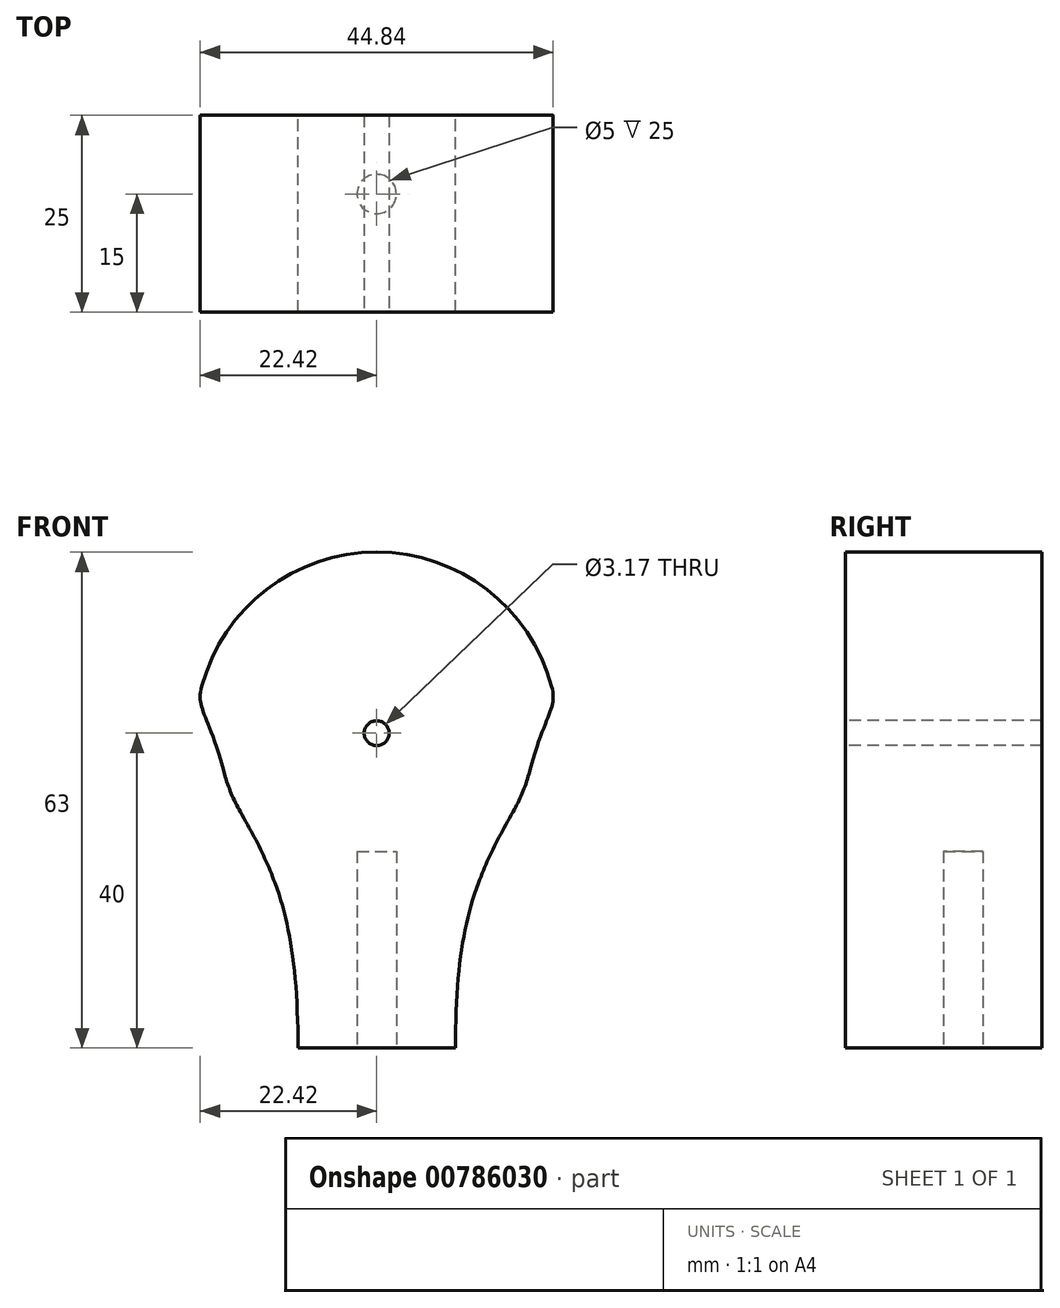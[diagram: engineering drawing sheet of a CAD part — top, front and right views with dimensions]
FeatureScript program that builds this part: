
annotation { "Feature Type Name" : "Feature", "Feature Type Description" : "" }
export const myFeature = defineFeature(function(context is Context, id is Id, definition is map)
    precondition{}
    {
        {
            var Q0;
            Q0=qCreatedBy(makeId("Front.planeOp"),FACE);
            var sketch = newSketch(context, id + "F0", { "sketchPlane" : qUnion([Q0])});
            skLineSegment(sketch, "E0.bottom", {"start": v(10, 0) * mm, "end": v(-10, 0) * mm, "construction": true});
            skLineSegment(sketch, "E0.top", {"start": v(10, -40) * mm, "end": v(-10, -40) * mm});
            skLineSegment(sketch, "E0.left", {"start": v(10, 0) * mm, "end": v(10, -40) * mm, "construction": true});
            skLineSegment(sketch, "E0.right", {"start": v(-10, 0) * mm, "end": v(-10, -40) * mm, "construction": true});
            skPoint(sketch, "E0.middle", {"position": v(0, -20) * mm});
            skCircle(sketch, "E1", {"center": v(0, 0) * mm, "radius": 20 * mm});
            skCircle(sketch, "E2", {"center": v(0, 0) * mm, "radius": 23 * mm});
            skLineSegment(sketch, "E3", {"start": v(0, 0) * mm, "end": v(22.22, 5.95) * mm});
            skLineSegment(sketch, "E4", {"start": v(0, 0) * mm, "end": v(19.32, -5.18) * mm});
            skLineSegment(sketch, "E5", {"start": v(0, 0) * mm, "end": v(17.32, -10) * mm});
            skLineSegment(sketch, "E6", {"start": v(0, 0) * mm, "end": v(19.92, 11.5) * mm});
            skFitSpline(sketch, "E7", {"points": [v(19.32, -5.18) * mm, v(22.22, 5.95) * mm], "startDerivative": vector(6.21, 23.18) * mm, "endDerivative": vector(-2.33, 8.7) * mm});
            skLineSegment(sketch, "E8", {"start": v(22.22, 5.95) * mm, "end": v(23, 3.06) * mm});
            skLineSegment(sketch, "E9", {"start": v(19.32, -5.18) * mm, "end": v(21.39, 2.55) * mm});
            skFitSpline(sketch, "E10", {"points": [v(17.32, -10) * mm, v(10, -40) * mm], "startDerivative": vector(-15, -25.98) * mm, "endDerivative": vector(0, -45) * mm});
            skLineSegment(sketch, "E11", {"start": v(17.32, -10) * mm, "end": v(12.32, -18.66) * mm});
            skLineSegment(sketch, "E12", {"start": v(0, -40) * mm, "end": v(0, 23) * mm, "construction": true});
            skFitSpline(sketch, "E13.MirrorCS", {"points": [v(-19.32, -5.18) * mm, v(-22.22, 5.95) * mm], "startDerivative": vector(-6.21, 23.18) * mm, "endDerivative": vector(2.33, 8.7) * mm});
            skFitSpline(sketch, "E14.MirrorCS", {"points": [v(-17.32, -10) * mm, v(-10, -40) * mm], "startDerivative": vector(15, -25.98) * mm, "endDerivative": vector(0, -45) * mm});
            skLineSegment(sketch, "E15.MirrorCS", {"start": v(0, 0) * mm, "end": v(-19.92, 11.5) * mm});
            skSolve(sketch);
        }
        {
            var Q0;
            {var subQ0=sQuery(id+"F0.wireOp",EDGE,"E6");var subQ1=sQuery(id+"F0.wireOp",EDGE,"E1");var subQ2=makeQuery(id+"F0.imprint","INTERSECT",VERTEX,{"derivedFrom":[subQ1,subQ0]});Q0=makeQuery(id+"F0.imprint","IMPRINT",FACE,{"disambiguationData":[TD([[makeQuery(id+"F0.imprint","IMPRINT",EDGE,{"disambiguationData":[TD([[subQ2,-1.0]])],"derivedFrom":subQ1}),1.0]])]});}
            var Q1;
            {var subQ0=sQuery(id+"F0.wireOp",EDGE,"E6");var subQ1=sQuery(id+"F0.wireOp",EDGE,"E1");var subQ2=makeQuery(id+"F0.imprint","INTERSECT",VERTEX,{"derivedFrom":[subQ1,subQ0]});Q1=makeQuery(id+"F0.imprint","IMPRINT",FACE,{"disambiguationData":[TD([[makeQuery(id+"F0.imprint","IMPRINT",EDGE,{"disambiguationData":[TD([[subQ2,-1.0]])],"derivedFrom":subQ1}),-1.0]])]});}
            var Q2;
            {var subQ0=sQuery(id+"F0.wireOp",EDGE,"E6");var subQ1=sQuery(id+"F0.wireOp",EDGE,"E1");var subQ2=makeQuery(id+"F0.imprint","INTERSECT",VERTEX,{"derivedFrom":[subQ1,subQ0]});Q2=makeQuery(id+"F0.imprint","IMPRINT",FACE,{"disambiguationData":[TD([[makeQuery(id+"F0.imprint","IMPRINT",EDGE,{"disambiguationData":[TD([[subQ2,1.0]])],"derivedFrom":subQ1}),-1.0]])]});}
            var Q3;
            {var subQ0=sQuery(id+"F0.wireOp",EDGE,"E6");var subQ1=sQuery(id+"F0.wireOp",EDGE,"E1");var subQ2=makeQuery(id+"F0.imprint","INTERSECT",VERTEX,{"derivedFrom":[subQ1,subQ0]});Q3=makeQuery(id+"F0.imprint","IMPRINT",FACE,{"disambiguationData":[TD([[makeQuery(id+"F0.imprint","IMPRINT",EDGE,{"disambiguationData":[TD([[subQ2,1.0]])],"derivedFrom":subQ1}),1.0]])]});}
            var Q4;
            {var subQ0=sQuery(id+"F0.wireOp",EDGE,"E4");Q4=makeQuery(id+"F0.imprint","IMPRINT",FACE,{"disambiguationData":[TD([[makeQuery(id+"F0.imprint","IMPRINT",EDGE,{"derivedFrom":subQ0}),1.0]])]});}
            var Q5;
            {var subQ0=sQuery(id+"F0.wireOp",EDGE,"E7");Q5=makeQuery(id+"F0.imprint","IMPRINT",FACE,{"disambiguationData":[TD([[makeQuery(id+"F0.imprint","IMPRINT",EDGE,{"derivedFrom":subQ0}),1.0]])]});}
            var Q6;
            {var subQ0=sQuery(id+"F0.wireOp",EDGE,"E4");Q6=makeQuery(id+"F0.imprint","IMPRINT",FACE,{"disambiguationData":[TD([[makeQuery(id+"F0.imprint","IMPRINT",EDGE,{"derivedFrom":subQ0}),-1.0]])]});}
            var Q7;
            {var subQ0=sQuery(id+"F0.wireOp",EDGE,"E5");Q7=makeQuery(id+"F0.imprint","IMPRINT",FACE,{"disambiguationData":[TD([[makeQuery(id+"F0.imprint","IMPRINT",EDGE,{"derivedFrom":subQ0}),-1.0]])]});}
            var Q8;
            {var subQ0=sQuery(id+"F0.wireOp",EDGE,"E0.top");Q8=makeQuery(id+"F0.imprint","IMPRINT",FACE,{"disambiguationData":[TD([[makeQuery(id+"F0.imprint","IMPRINT",EDGE,{"derivedFrom":subQ0}),-1.0]])]});}
            var Q9;
            {var subQ3=sQuery(id+"F0.wireOp",EDGE,"E14.MirrorCS");var subQ5=sQuery(id+"F0.wireOp",EDGE,"E2");var subQ6=makeQuery(id+"F0.imprint","INTERSECT",VERTEX,{"derivedFrom":[subQ5,subQ3]});Q9=makeQuery(id+"F0.imprint","IMPRINT",FACE,{"disambiguationData":[TD([[makeQuery(id+"F0.imprint","IMPRINT",EDGE,{"disambiguationData":[TD([[subQ6,-1.0]])],"derivedFrom":subQ5}),1.0]])]});}
            var Q10;
            {var subQ0=sQuery(id+"F0.wireOp",EDGE,"E13.MirrorCS");Q10=makeQuery(id+"F0.imprint","IMPRINT",FACE,{"disambiguationData":[TD([[makeQuery(id+"F0.imprint","IMPRINT",EDGE,{"derivedFrom":subQ0}),-1.0]])]});}
            extrude(context, id + "F1", {"entities" : qUnion([Q0, Q1, Q2, Q3, Q4, Q5, Q6, Q7, Q8, Q9, Q10]), "depth" : 25 * mm, "offsetDistance" : 25 * mm});
        }
        {
            var Q0;
            Q0=makeQuery(id+"F1.opExtrude","CAP_FACE",FACE,{"disambiguationData":[OSD([sQuery(id+"F0.wireOp",EDGE,"E0.top"),sQuery(id+"F0.wireOp",EDGE,"E1"),sQuery(id+"F0.wireOp",EDGE,"E2"),sQuery(id+"F0.wireOp",EDGE,"E7"),sQuery(id+"F0.wireOp",EDGE,"E10"),sQuery(id+"F0.wireOp",EDGE,"E13.MirrorCS"),sQuery(id+"F0.wireOp",EDGE,"E14.MirrorCS")])],"isStart":false});
            var sketch = newSketch(context, id + "F2", { "sketchPlane" : qUnion([Q0])});
            skCircle(sketch, "E16", {"center": v(0, 0) * mm, "radius": 1.59 * mm});
            skSolve(sketch);
        }
        {
            var Q0;
            Q0=qSketchRegion(id+"F2",true);
            extrude(context, id + "F3", {"entities" : qUnion([Q0]), "operationType" : NewBodyOperationType.REMOVE, "oppositeDirection" : true, "depth" : 25 * mm, "offsetDistance" : 25 * mm});
        }
        {
            var Q0;
            Q0=makeQuery(id+"F1.opExtrude","SWEPT_FACE",FACE,{"disambiguationData":[OSD([sQuery(id+"F0.wireOp",EDGE,"E0.top")])]});
            var sketch = newSketch(context, id + "F4", { "sketchPlane" : qUnion([Q0])});
            skCircle(sketch, "E17", {"center": v(0, 10) * mm, "radius": 2.5 * mm});
            skSolve(sketch);
        }
        {
            var Q0;
            Q0=qSketchRegion(id+"F4",true);
            extrude(context, id + "F5", {"entities" : qUnion([Q0]), "operationType" : NewBodyOperationType.REMOVE, "oppositeDirection" : true, "depth" : 25 * mm, "offsetDistance" : 25 * mm});
        }
    });
